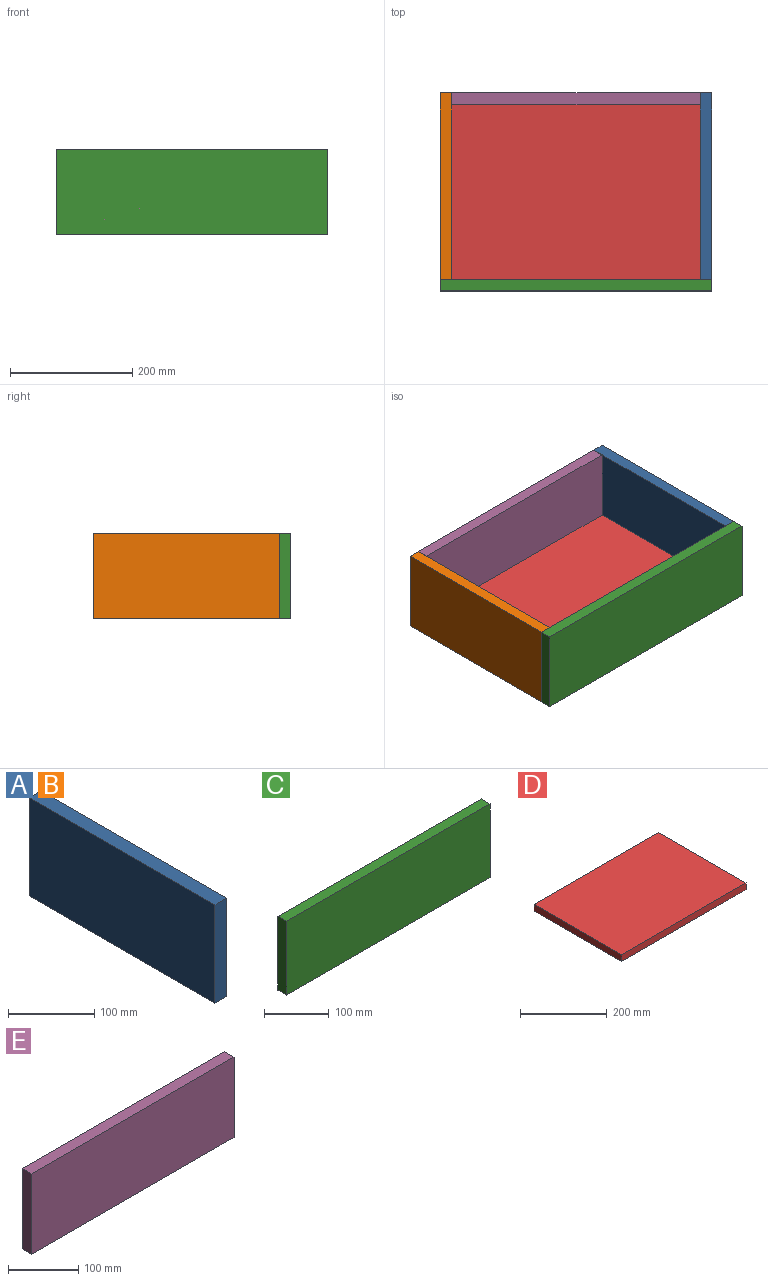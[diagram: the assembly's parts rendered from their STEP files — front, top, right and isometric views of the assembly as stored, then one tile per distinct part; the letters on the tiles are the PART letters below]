
ASSEMBLY  parts=5 mates=4
PART A: 6 faces, bbox 19.1x304.8x139.7 mm
  f0: plane 139.7x19.05mm, normal (0,-1,0), area 2661.3mm2, adj f1,f3,f4,f5
  f1: plane 304.8x139.7mm, normal (1,0,0), area 42580.6mm2, adj f0,f2,f4,f5
  f2: plane 139.7x19.05mm, normal (0,1,0), area 2661.3mm2, adj f1,f3,f4,f5
  f3: plane 304.8x139.7mm, normal (-1,0,0), area 42580.6mm2, adj f0,f2,f4,f5
  f4: plane 304.8x19.05mm, normal (0,0,1), area 5806.4mm2, adj f0,f1,f2,f3
  f5: plane 304.8x19.05mm, normal (0,0,-1), area 5806.4mm2, adj f0,f1,f2,f3
PART B: same geometry as A
PART C: 6 faces, bbox 444.5x19.1x139.7 mm
  f0: plane 444.5x139.7mm, normal (0,1,0), area 62096.6mm2, adj f1,f3,f4,f5
  f1: plane 139.7x19.05mm, normal (-1,0,0), area 2661.3mm2, adj f0,f2,f4,f5
  f2: plane 444.5x139.7mm, normal (0,-1,0), area 62096.6mm2, adj f1,f3,f4,f5
  f3: plane 139.7x19.05mm, normal (1,0,0), area 2661.3mm2, adj f0,f2,f4,f5
  f4: plane 444.5x19.05mm, normal (0,0,1), area 8467.7mm2, adj f0,f1,f2,f3
  f5: plane 444.5x19.05mm, normal (0,0,-1), area 8467.7mm2, adj f0,f1,f2,f3
PART D: 6 faces, bbox 406.4x285.8x19.1 mm
  f0: plane 406.4x19.05mm, normal (0,-1,0), area 7741.9mm2, adj f1,f3,f4,f5
  f1: plane 285.75x19.05mm, normal (1,0,0), area 5443.5mm2, adj f0,f2,f4,f5
  f2: plane 406.4x19.05mm, normal (0,1,0), area 7741.9mm2, adj f1,f3,f4,f5
  f3: plane 285.75x19.05mm, normal (-1,0,0), area 5443.5mm2, adj f0,f2,f4,f5
  f4: plane 406.4x285.75mm, normal (0,0,1), area 116128.8mm2, adj f0,f1,f2,f3
  f5: plane 406.4x285.75mm, normal (0,0,-1), area 116128.8mm2, adj f0,f1,f2,f3
PART E: 6 faces, bbox 406.4x19.1x139.7 mm
  f0: plane 406.4x139.7mm, normal (0,1,0), area 56774.1mm2, adj f1,f3,f4,f5
  f1: plane 139.7x19.05mm, normal (-1,0,0), area 2661.3mm2, adj f0,f2,f4,f5
  f2: plane 406.4x139.7mm, normal (0,-1,0), area 56774.1mm2, adj f1,f3,f4,f5
  f3: plane 139.7x19.05mm, normal (1,0,0), area 2661.3mm2, adj f0,f2,f4,f5
  f4: plane 406.4x19.05mm, normal (0,0,1), area 7741.9mm2, adj f0,f1,f2,f3
  f5: plane 406.4x19.05mm, normal (0,0,-1), area 7741.9mm2, adj f0,f1,f2,f3
PLACE A t=(309.09,72.08,-51.22)mm
PLACE B t=(-116.36,72.08,-51.22)mm
PLACE C t=(-135.41,72.08,-51.22)mm
PLACE D t=(290.04,72.08,-51.22)mm
PLACE E t=(-116.36,376.88,-51.22)mm
MATE fastened E.f2 <-> D.f2  axis (0,-1,0) through (290.04,357.83,-51.22)mm
MATE fastened B.f1 <-> D.f3  axis (1,0,0) through (-116.36,72.08,-51.22)mm
MATE fastened D.f0 <-> C.f0  axis (0,-1,0) through (290.04,72.08,-51.22)mm
MATE fastened A.f3 <-> D.f1  axis (-1,0,0) through (290.04,72.08,-51.22)mm
